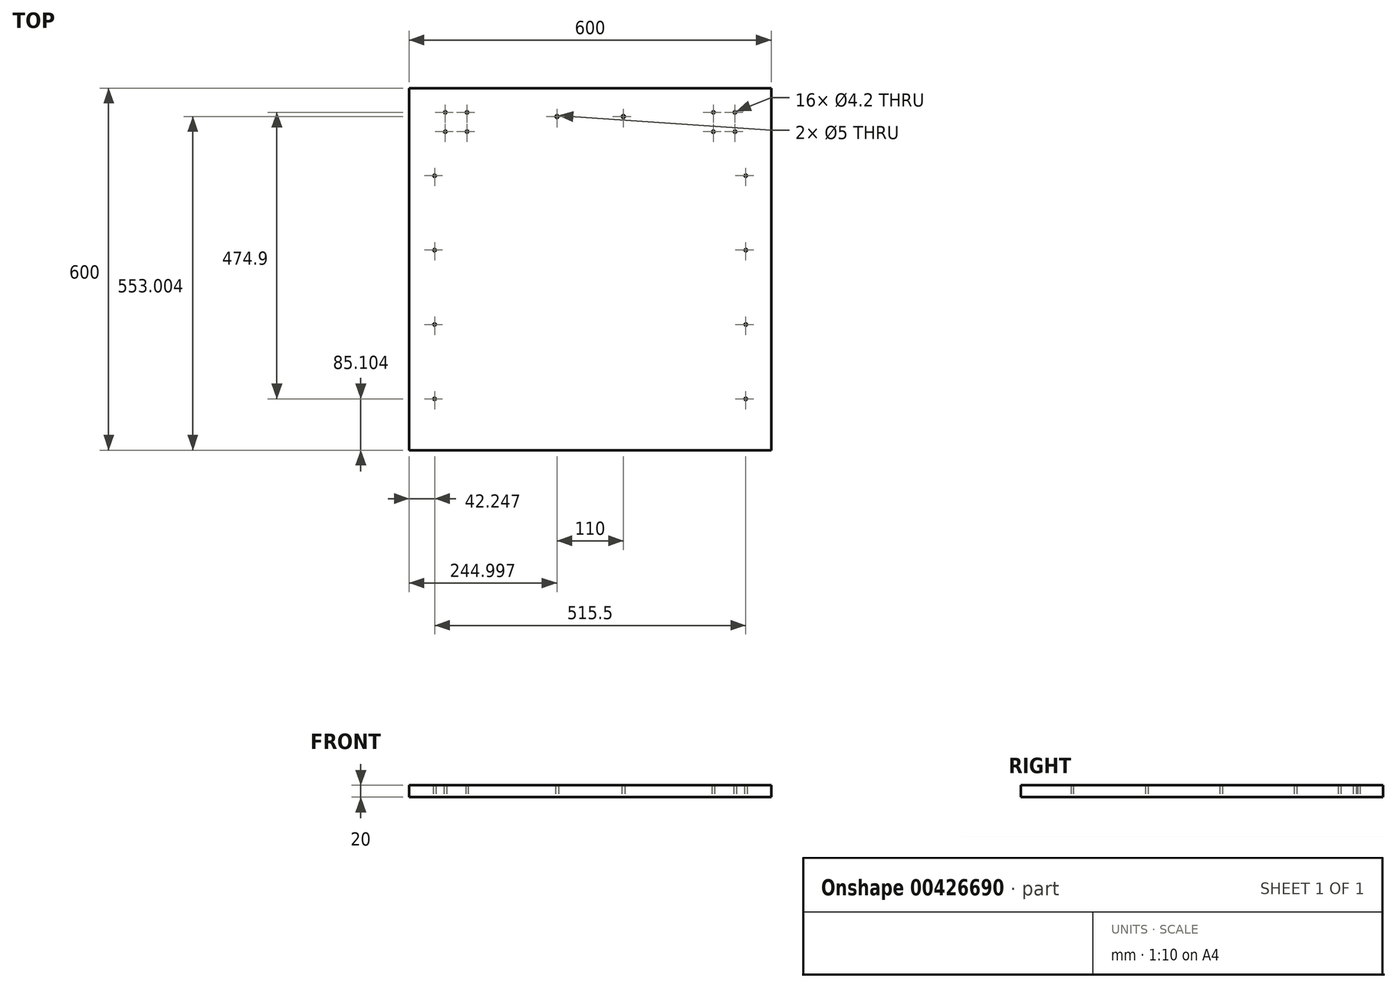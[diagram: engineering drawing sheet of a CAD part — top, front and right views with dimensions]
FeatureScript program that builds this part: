
annotation { "Feature Type Name" : "Feature", "Feature Type Description" : "" }
export const myFeature = defineFeature(function(context is Context, id is Id, definition is map)
    precondition{}
    {
        {
            var Q0;
            Q0=qCreatedBy(makeId("Top.planeOp"),FACE);
            var sketch = newSketch(context, id + "F0", { "sketchPlane" : qUnion([Q0])});
            skLineSegment(sketch, "E0.bottom", {"start": v(-722.9, 558) * mm, "end": v(-122.9, 558) * mm});
            skLineSegment(sketch, "E0.top", {"start": v(-722.9, -42) * mm, "end": v(-122.9, -42) * mm});
            skLineSegment(sketch, "E0.left", {"start": v(-722.9, 558) * mm, "end": v(-722.9, -42) * mm});
            skLineSegment(sketch, "E0.right", {"start": v(-122.9, 558) * mm, "end": v(-122.9, -42) * mm});
            skLineSegment(sketch, "E1.0", {"start": v(-422.9, 521) * mm, "end": v(-422.9, -42) * mm});
            skPoint(sketch, "E2", {"position": v(-477.9, 511) * mm});
            skPoint(sketch, "E3", {"position": v(-367.9, 511) * mm});
            skPoint(sketch, "E4", {"position": v(-680.64, 413) * mm});
            skPoint(sketch, "E5", {"position": v(-680.64, 289.7) * mm});
            skPoint(sketch, "E6", {"position": v(-680.64, 166.4) * mm});
            skPoint(sketch, "E7", {"position": v(-680.64, 43.1) * mm});
            skPoint(sketch, "E8", {"position": v(-165.14, 413) * mm});
            skPoint(sketch, "E9", {"position": v(-165.14, 289.7) * mm});
            skPoint(sketch, "E10", {"position": v(-165.14, 166.4) * mm});
            skPoint(sketch, "E11", {"position": v(-165.14, 43.1) * mm});
            skPoint(sketch, "E12", {"position": v(-662.9, 518) * mm});
            skPoint(sketch, "E13", {"position": v(-626.9, 518) * mm});
            skPoint(sketch, "E14", {"position": v(-626.9, 486) * mm});
            skPoint(sketch, "E15", {"position": v(-662.9, 486) * mm});
            skPoint(sketch, "E16", {"position": v(-218.9, 518) * mm});
            skPoint(sketch, "E17", {"position": v(-182.9, 518) * mm});
            skPoint(sketch, "E18", {"position": v(-182.9, 486) * mm});
            skPoint(sketch, "E19", {"position": v(-218.9, 486) * mm});
            skSolve(sketch);
        }
        {
            var Q0;
            {var subQ0=sQuery(id+"F0.wireOp",EDGE,"E0.left");Q0=makeQuery(id+"F0.imprint","IMPRINT",FACE,{"disambiguationData":[TD([[makeQuery(id+"F0.imprint","IMPRINT",EDGE,{"derivedFrom":subQ0}),1.0]])]});}
            var Q1;
            {var subQ0=sQuery(id+"F0.wireOp",EDGE,"E0.right");Q1=makeQuery(id+"F0.imprint","IMPRINT",FACE,{"disambiguationData":[TD([[makeQuery(id+"F0.imprint","IMPRINT",EDGE,{"derivedFrom":subQ0}),-1.0]])]});}
            extrude(context, id + "F1", {"entities" : qUnion([Q0, Q1]), "depth" : 20 * mm});
        }
        {
            var Q0;
            Q0=sQuery(id+"F0.wireOp",VERTEX,"E2");
            var Q1;
            Q1=sQuery(id+"F0.wireOp",VERTEX,"E3");
            var Q2;
            Q2=makeQuery(id+"F1.opExtrude","SWEPT_BODY",BODY,{"disambiguationData":[OSD([sQuery(id+"F0.wireOp",EDGE,"E0.bottom"),sQuery(id+"F0.wireOp",EDGE,"E0.top"),sQuery(id+"F0.wireOp",EDGE,"E0.left"),sQuery(id+"F0.wireOp",EDGE,"E0.right")])]});
            hole(context, id + "F2", {"style" : HoleStyle.SIMPLE, "endStyle" : HoleEndStyle.THROUGH, "oppositeDirection" : true, "standardTappedOrClearance" : lookupTablePath({ "standard" : "ISO", "engagement" : "75%", "pitch" : "1 mm", "size" : "M6", "type" : "Tapped" }), "standardBlindInLast" : lookupTablePath({ "standard" : "ISO", "engagement" : "75%", "pitch" : "1 mm", "size" : "M6", "type" : "Tapped" }), "holeDiameter" : 5 * mm, "showTappedDepth" : true, "isTappedThrough" : true, "tappedDepth" : 10 * mm, "tapClearance" : 3, "locations" : qUnion([Q0, Q1]), "scope" : qUnion([Q2]), "majorDiameter" : 6 * mm});
        }
        {
            var Q0;
            Q0=sQuery(id+"F0.wireOp",VERTEX,"E4");
            var Q1;
            Q1=sQuery(id+"F0.wireOp",VERTEX,"E5");
            var Q2;
            Q2=sQuery(id+"F0.wireOp",VERTEX,"E6");
            var Q3;
            Q3=sQuery(id+"F0.wireOp",VERTEX,"E7");
            var Q4;
            Q4=sQuery(id+"F0.wireOp",VERTEX,"E11");
            var Q5;
            Q5=sQuery(id+"F0.wireOp",VERTEX,"E10");
            var Q6;
            Q6=sQuery(id+"F0.wireOp",VERTEX,"E9");
            var Q7;
            Q7=sQuery(id+"F0.wireOp",VERTEX,"E8");
            var Q8;
            Q8=makeQuery(id+"F1.opExtrude","SWEPT_BODY",BODY,{"disambiguationData":[OSD([sQuery(id+"F0.wireOp",EDGE,"E0.bottom"),sQuery(id+"F0.wireOp",EDGE,"E0.top"),sQuery(id+"F0.wireOp",EDGE,"E0.left"),sQuery(id+"F0.wireOp",EDGE,"E0.right")])]});
            hole(context, id + "F3", {"style" : HoleStyle.SIMPLE, "endStyle" : HoleEndStyle.THROUGH, "oppositeDirection" : true, "standardTappedOrClearance" : lookupTablePath({ "standard" : "ISO", "engagement" : "75%", "pitch" : "0.8 mm", "size" : "M5", "type" : "Tapped" }), "standardBlindInLast" : lookupTablePath({ "standard" : "ISO", "engagement" : "75%", "pitch" : "0.8 mm", "size" : "M5", "type" : "Tapped" }), "holeDiameter" : 4.2 * mm, "showTappedDepth" : true, "isTappedThrough" : true, "tappedDepth" : 10 * mm, "tapClearance" : 3, "locations" : qUnion([Q0, Q1, Q2, Q3, Q4, Q5, Q6, Q7]), "scope" : qUnion([Q8]), "majorDiameter" : 5 * mm});
        }
        {
            var Q0;
            Q0=sQuery(id+"F0.wireOp",VERTEX,"E14");
            var Q1;
            Q1=sQuery(id+"F0.wireOp",VERTEX,"E15");
            var Q2;
            Q2=sQuery(id+"F0.wireOp",VERTEX,"E12");
            var Q3;
            Q3=sQuery(id+"F0.wireOp",VERTEX,"E13");
            var Q4;
            Q4=sQuery(id+"F0.wireOp",VERTEX,"E16");
            var Q5;
            Q5=sQuery(id+"F0.wireOp",VERTEX,"E17");
            var Q6;
            Q6=sQuery(id+"F0.wireOp",VERTEX,"E18");
            var Q7;
            Q7=sQuery(id+"F0.wireOp",VERTEX,"E19");
            var Q8;
            Q8=makeQuery(id+"F1.opExtrude","SWEPT_BODY",BODY,{"disambiguationData":[OSD([sQuery(id+"F0.wireOp",EDGE,"E0.bottom"),sQuery(id+"F0.wireOp",EDGE,"E0.top"),sQuery(id+"F0.wireOp",EDGE,"E0.left"),sQuery(id+"F0.wireOp",EDGE,"E0.right")])]});
            hole(context, id + "F4", {"style" : HoleStyle.SIMPLE, "endStyle" : HoleEndStyle.THROUGH, "oppositeDirection" : true, "standardTappedOrClearance" : lookupTablePath({ "standard" : "ISO", "engagement" : "75%", "pitch" : "0.8 mm", "size" : "M5", "type" : "Tapped" }), "standardBlindInLast" : lookupTablePath({ "standard" : "ISO", "engagement" : "75%", "pitch" : "0.8 mm", "size" : "M5", "type" : "Tapped" }), "holeDiameter" : 4.2 * mm, "showTappedDepth" : true, "isTappedThrough" : true, "tappedDepth" : 10 * mm, "tapClearance" : 3, "locations" : qUnion([Q0, Q1, Q2, Q3, Q4, Q5, Q6, Q7]), "scope" : qUnion([Q8]), "majorDiameter" : 5 * mm});
        }
    });
